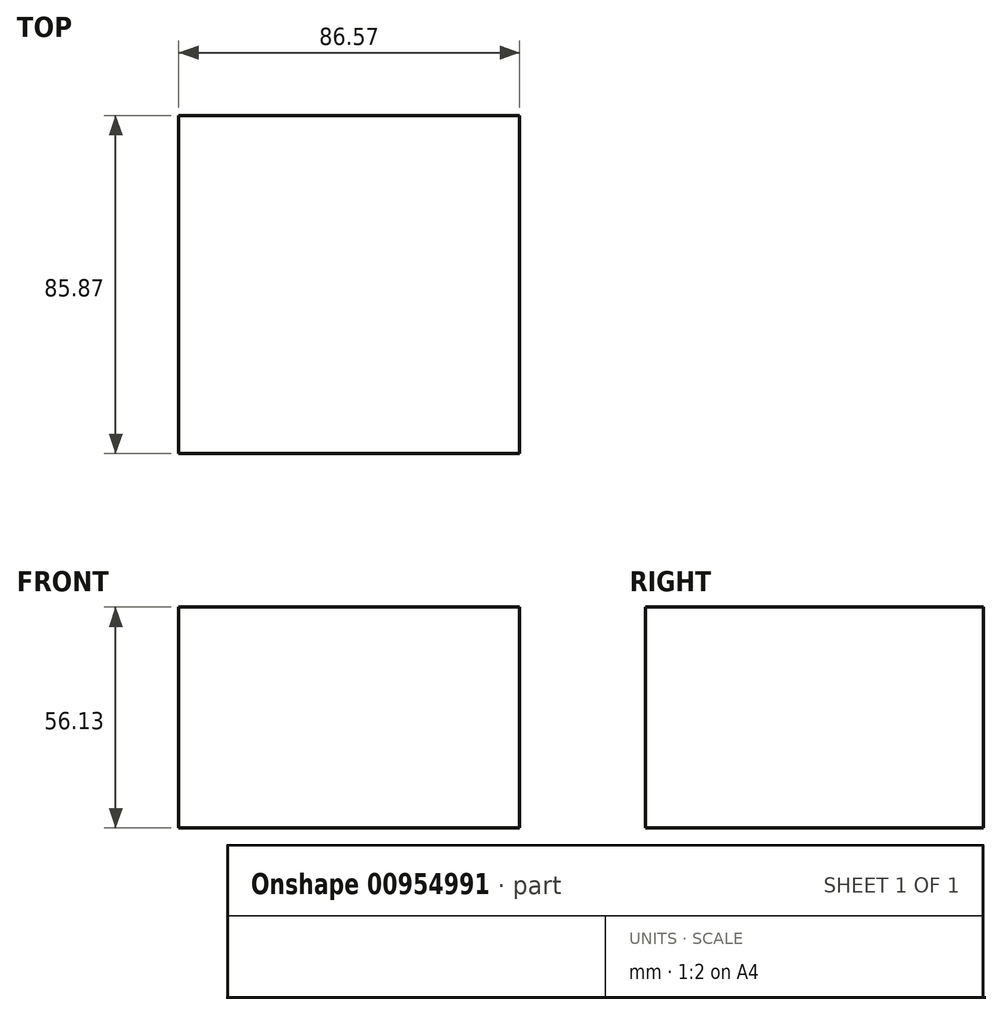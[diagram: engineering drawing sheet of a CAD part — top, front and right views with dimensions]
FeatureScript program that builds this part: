
annotation { "Feature Type Name" : "Feature", "Feature Type Description" : "" }
export const myFeature = defineFeature(function(context is Context, id is Id, definition is map)
    precondition{}
    {
        {
            var Q0;
            Q0=qCreatedBy(makeId("Top.planeOp"),FACE);
            var sketch = newSketch(context, id + "F0", { "sketchPlane" : qUnion([Q0])});
            skLineSegment(sketch, "E0.bottom", {"start": v(-54.45, 49.04) * mm, "end": v(32.12, 49.04) * mm});
            skLineSegment(sketch, "E0.top", {"start": v(-54.45, -36.83) * mm, "end": v(32.12, -36.83) * mm});
            skLineSegment(sketch, "E0.left", {"start": v(-54.45, 49.04) * mm, "end": v(-54.45, -36.83) * mm});
            skLineSegment(sketch, "E0.right", {"start": v(32.12, 49.04) * mm, "end": v(32.12, -36.83) * mm});
            skSolve(sketch);
        }
        {
            var Q0;
            Q0=makeQuery(id+"F0.imprint","IMPRINT",FACE,{"disambiguationData":[TD([[makeQuery(id+"F0.imprint","IMPRINT",EDGE,{"derivedFrom":sQuery(id+"F0.wireOp",EDGE,"E0.bottom")}),-1.0]])]});
            extrude(context, id + "F1", {"entities" : qUnion([Q0]), "depth" : 56.13 * mm, "offsetDistance" : 25.4 * mm});
        }
    });
